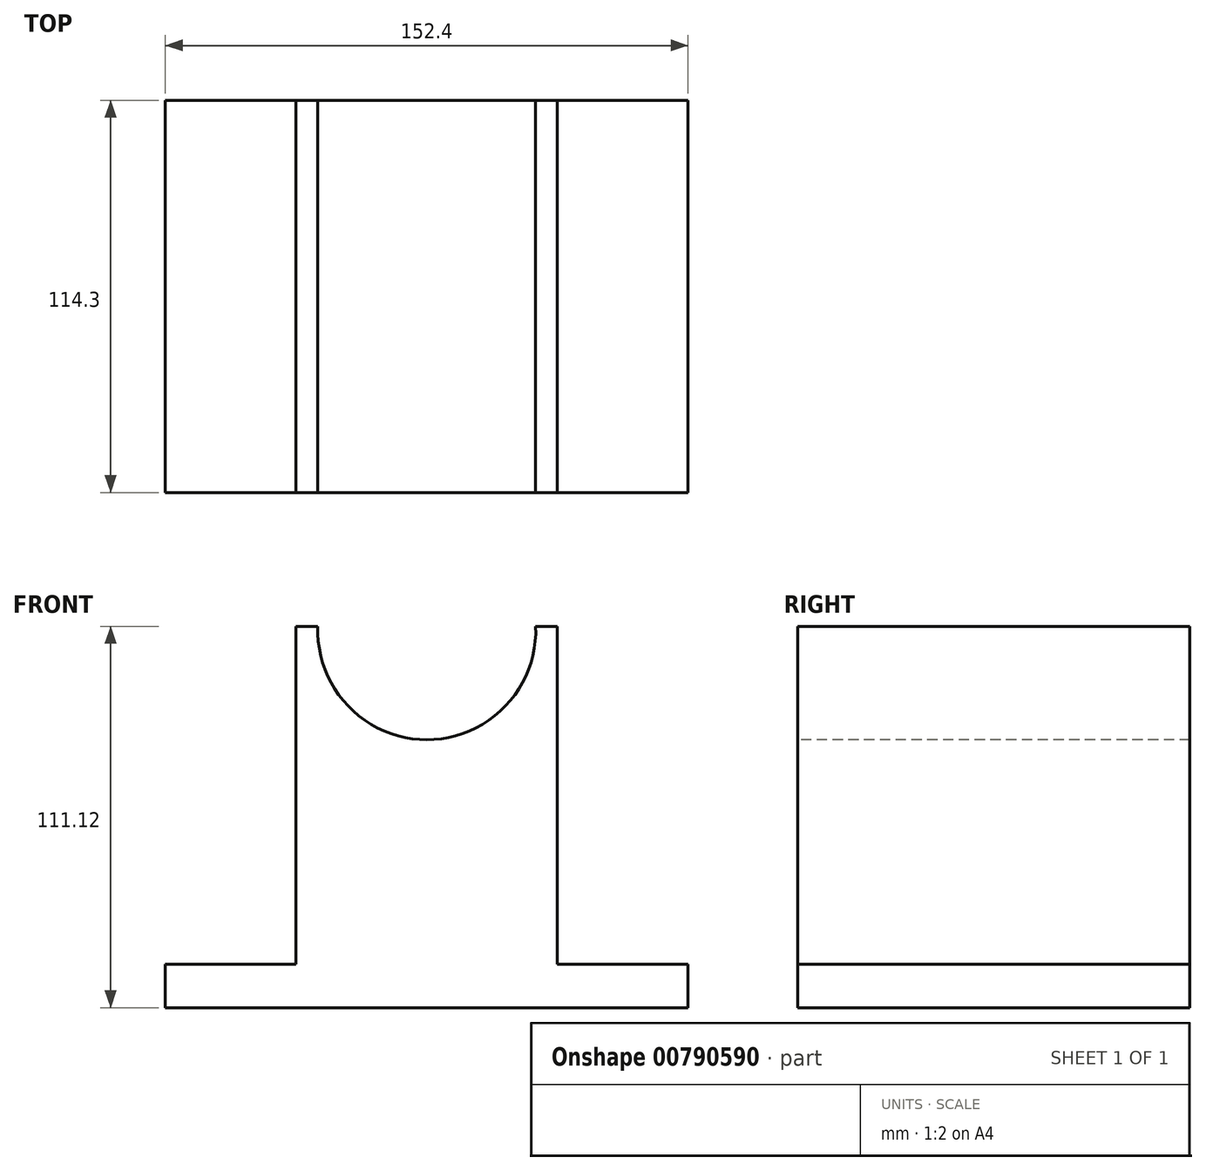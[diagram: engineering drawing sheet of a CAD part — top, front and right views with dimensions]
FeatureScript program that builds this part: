
annotation { "Feature Type Name" : "Feature", "Feature Type Description" : "" }
export const myFeature = defineFeature(function(context is Context, id is Id, definition is map)
    precondition{}
    {
        {
            var Q0;
            Q0=qCreatedBy(makeId("Front.planeOp"),FACE);
            var sketch = newSketch(context, id + "F0", { "sketchPlane" : qUnion([Q0])});
            skLineSegment(sketch, "E0", {"start": v(0, 0) * mm, "end": v(152.4, 0) * mm});
            skLineSegment(sketch, "E1", {"start": v(152.4, 0) * mm, "end": v(152.4, 12.7) * mm});
            skLineSegment(sketch, "E2", {"start": v(152.4, 12.7) * mm, "end": v(114.3, 12.7) * mm});
            skLineSegment(sketch, "E3", {"start": v(0, 0) * mm, "end": v(0, 12.7) * mm});
            skLineSegment(sketch, "E4", {"start": v(0, 12.7) * mm, "end": v(38.1, 12.7) * mm});
            skLineSegment(sketch, "E5", {"start": v(38.1, 12.7) * mm, "end": v(38.1, 111.12) * mm});
            skLineSegment(sketch, "E6", {"start": v(38.1, 111.12) * mm, "end": v(114.3, 111.12) * mm});
            skLineSegment(sketch, "E7", {"start": v(114.3, 111.12) * mm, "end": v(114.3, 12.7) * mm});
            skSolve(sketch);
        }
        {
            var Q0;
            Q0=makeQuery(id+"F0.imprint","IMPRINT",FACE,{"disambiguationData":[TD([[makeQuery(id+"F0.imprint","IMPRINT",EDGE,{"derivedFrom":sQuery(id+"F0.wireOp",EDGE,"E0")}),1.0]])]});
            extrude(context, id + "F1", {"entities" : qUnion([Q0]), "depth" : 114.3 * mm, "offsetDistance" : 25.4 * mm});
        }
        {
            var Q0;
            Q0=makeQuery(id+"F1.opExtrude","CAP_FACE",FACE,{"disambiguationData":[OSD([sQuery(id+"F0.wireOp",EDGE,"E0"),sQuery(id+"F0.wireOp",EDGE,"E1"),sQuery(id+"F0.wireOp",EDGE,"E2"),sQuery(id+"F0.wireOp",EDGE,"E3"),sQuery(id+"F0.wireOp",EDGE,"E4"),sQuery(id+"F0.wireOp",EDGE,"E5"),sQuery(id+"F0.wireOp",EDGE,"E6"),sQuery(id+"F0.wireOp",EDGE,"E7")])],"isStart":false});
            var sketch = newSketch(context, id + "F2", { "sketchPlane" : qUnion([Q0])});
            skLineSegment(sketch, "E8", {"start": v(76.2, 111.12) * mm, "end": v(107.95, 111.12) * mm, "construction": true});
            skLineSegment(sketch, "E9", {"start": v(76.2, 111.12) * mm, "end": v(44.45, 111.12) * mm, "construction": true});
            skArc(sketch, "E10", {"start": v(44.45, 111.12) * mm, "mid": v(76.2, 78.09) * mm, "end": v(107.95, 111.12) * mm});
            skSolve(sketch);
        }
        {
            var Q0;
            {var subQ0=sQuery(id+"F2.wireOp",EDGE,"E10");Q0=makeQuery(id+"F2.imprint","IMPRINT",FACE,{"disambiguationData":[TD([[makeQuery(id+"F2.imprint","IMPRINT",EDGE,{"derivedFrom":subQ0}),1.0]])]});}
            extrude(context, id + "F3", {"entities" : qUnion([Q0]), "operationType" : NewBodyOperationType.REMOVE, "oppositeDirection" : true, "depth" : 114.3 * mm, "offsetDistance" : 25.4 * mm});
        }
    });
